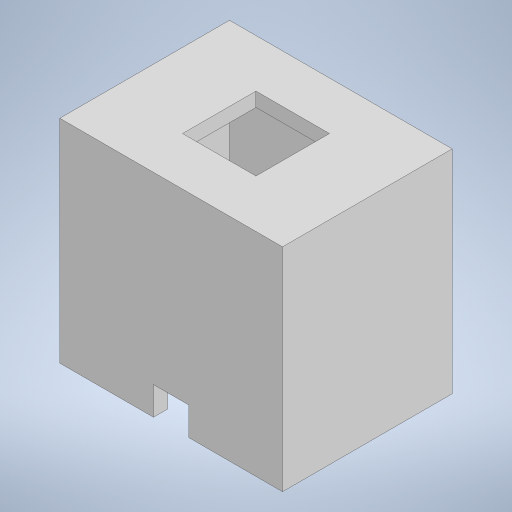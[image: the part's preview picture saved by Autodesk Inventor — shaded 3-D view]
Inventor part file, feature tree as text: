
AUTODESK INVENTOR PART (.ipt)
format: ipt  version: 2023 (Build 270158000, 158)  size: 209,408 bytes
history: native  units: in
note: dims shown in document units (in); Inventor stores cm internally (conversion verified against a paired STEP export)
features: extrude x3, sketch x3, projected_geometry x2
ambient origin geometry x8: Origin, YZ Plane, XZ Plane, XY Plane, X Axis, Y Axis, Z Axis, Center Point
bodies: Solid1 (feature_tree)
feature tree (8):
  extrude  "Extrusion1"  Depth=0.6875in
  extrude  "Extrusion2"  Depth=0.3438in
  extrude  "Extrusion3"  Depth=0.05in
  sketch  "Sketch1"  dims[d0=0.5in d1=0.6875in]
  sketch  "Sketch2"  dims[d2=0.25in d3=0.3438in]
  projected_geometry  "Projected Loop1"
  sketch  "Sketch3"  dims[d4=0.05in d5=0.0in d7=0.05in d8=0.75in d9=0.0in d10=0.125in d11=0.7875in d12=0.3938in d13=0.1in d14=0.15in d15=0.0in d16=0.26in d17=0.26in d18=0.13in d19=0.13in]
  projected_geometry  "Projected Loop2"
